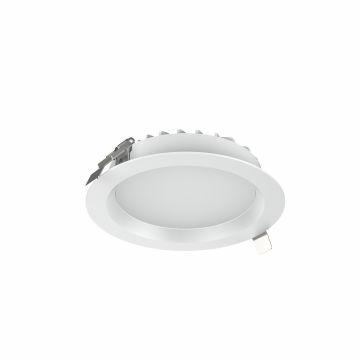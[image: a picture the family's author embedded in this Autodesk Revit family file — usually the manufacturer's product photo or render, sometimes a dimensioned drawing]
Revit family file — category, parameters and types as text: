
# Revit family: Lighting-Terziario-GEWISS-ELIA-DL-LED_INCASSO
name_source: partatom
category: Apparecchi per illuminazione
units: mm (PartAtom-declared; Revit-internal decimal feet)

## family parameters
Condiviso = No
Host = Superficie
Punto di calcolo locali = Sì
Quota connettore circolare = Usa diametro
Sorgente d'illuminazione = Sì
Taglio con vuoti quando caricato = No
Tipo di parte = Normale

## types (8) — shared parameters
Angolo inclinazione = -90.00°
Applicazione = Interno
Catalogo = LIGHTING
Catalogo Serie = ELIA DL
Classe isolamento = II
Colore = Bianco
Dimensioni (mm) = Standard
Emetti da lunghezza linea = 610 mm
FORO_CONTROSOFFITTO = 80 mm  [stored 0.262467 ft]
File diagramma fotometrico = GWF1511QA940.IES
Filtro dei colori = 16777215
Garanzia = 5 anni
Grado di protezione = IP40 - IP54
IDF = e32dd34c-8be7-4b35-b70e-442f7a3c5db5
IDT = 67a9fb0b-5b9a-414d-aab5-ce16ea450aa5
Immagine tipo = ELIA_DL.jpg
Installazione = Incasso modulare
LARGHEZZA_FORO = 820 mm
LED = <Per categoria>
LED Life time (L80B50) = L80 B50 (Tq25°) = 50.000h
LUNGHEZZA FORO = 969 mm
L_lampada = 1500 mm  [stored 4.92126 ft]
Lampada: = LED
Ottica = Opale diffondente
POSIZIONE = 80000
Peso (kg) = 0,8
Peso (kg): = 0,8
Produttore = GEWISS S.p.A.
Prospetto di default = 1219 mm
Resistenza agli urti = IK06
SEO = Incasso modulare
STRUTTURA = <Per categoria>
Scheda Tecnica = https://www.gewiss.com
Temperatura di colore = 4000K
Temperatura di colore: = 4000K
Temperatura di funzionamento = -20° +45°
Temperatura di utilizzo = -20° +45°
Tensione = 220-240 VÂ
Tipo lampada = LED
Tipologia = Incasso modulare
Tipologia sorgente luminosa = LED - Non sostituibile
URL = https://www.gewiss.com
Variazione temperatura colore lampada con luminosità attenuata = <Nessuno>
Versione file RFA = 20.0

## per-type parameters (varying)
| type | Descrizione | Lumen output (lm) | Modello | Potenza di sistema |
| GWF1511MA940 - ELIA DL M2 40K OPAL DALI CRI90 | ELIA DL M2 40K OPAL DALI CRI90 | 2340 | GWF1511MA940 | 25W |
| GWF1510MA940 - ELIA DL M2 40K  OPAL ON/OFF CRI90 | ELIA DL M2 40K  OPAL ON/OFF CRI90 | 2340 | GWF1510MA940 | 25W |
| GWF1511QA940 - ELIA DL L2 40K OPAL DALI CRI90 | ELIA DL L2 40K OPAL DALI CRI90 | 3200 | GWF1511QA940 | 35W |
| GWF1510QA840 - ELIA DL L2 40K  OPAL ON/OFF CRI80 | ELIA DL L2 40K  OPAL ON/OFF CRI80 | 3550 | GWF1510QA840 | 35W |
| GWF1510MA840 - ELIA DL M2 40K OPAL ON/OFF CRI80 | ELIA DL M2 40K OPAL ON/OFF CRI80 | 2600 | GWF1510MA840 | 25W |
| GWF1511QA840 - ELIA DL L2 40K OPAL DALI CRI80 | ELIA DL L2 40K OPAL DALI CRI80 | 3550 | GWF1511QA840 | 35W |
| GWF1511MA840 - ELIA DL M2 40K OPAL DALI CRI80 | ELIA DL M2 40K OPAL DALI CRI80 | 2600 | GWF1511MA840 | 25W |
| GWF1510QA940 - ELIA DL L2 40K  OPAL ON/OFF CRI90 | ELIA DL L2 40K  OPAL ON/OFF CRI90 | 3200 | GWF1510QA940 | 35W |

note: [stored X ft] marks values corroborated as IEEE doubles in the binary element streams (Revit-internal decimal feet)
